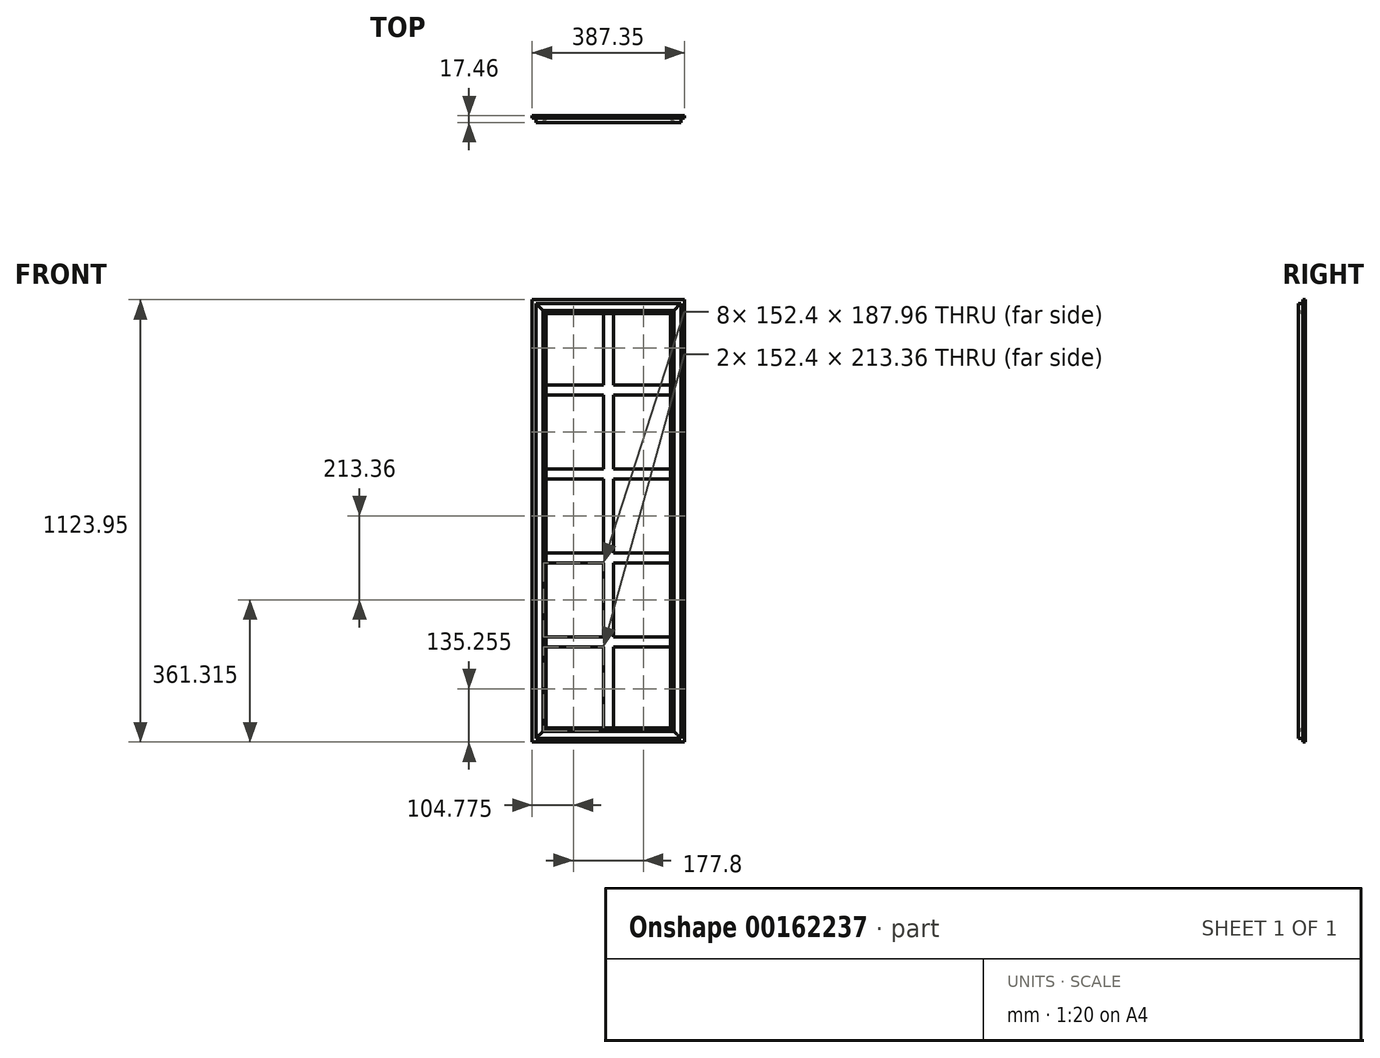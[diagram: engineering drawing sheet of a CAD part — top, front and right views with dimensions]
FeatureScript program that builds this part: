
annotation { "Feature Type Name" : "Feature", "Feature Type Description" : "" }
export const myFeature = defineFeature(function(context is Context, id is Id, definition is map)
    precondition{}
    {
        {
            var Q0;
            Q0=qCreatedBy(makeId("Front.planeOp"),FACE);
            var sketch = newSketch(context, id + "F0", { "sketchPlane" : qUnion([Q0])});
            skLineSegment(sketch, "E0.bottom", {"start": v(0, 1123.95) * mm, "end": v(387.35, 1123.95) * mm});
            skLineSegment(sketch, "E0.top", {"start": v(0, 0) * mm, "end": v(387.35, 0) * mm});
            skLineSegment(sketch, "E0.left", {"start": v(0, 1123.95) * mm, "end": v(0, 0) * mm});
            skLineSegment(sketch, "E0.right", {"start": v(387.35, 1123.95) * mm, "end": v(387.35, 0) * mm});
            skSolve(sketch);
        }
        {
            var Q0;
            Q0=qSketchRegion(id+"F0",true);
            extrude(context, id + "F1", {"entities" : qUnion([Q0]), "depth" : 6.35 * mm});
        }
        {
            var Q0;
            Q0=makeQuery(id+"F1.opExtrude","CAP_FACE",FACE,{"disambiguationData":[OSD([sQuery(id+"F0.wireOp",EDGE,"E0.bottom"),sQuery(id+"F0.wireOp",EDGE,"E0.top"),sQuery(id+"F0.wireOp",EDGE,"E0.left"),sQuery(id+"F0.wireOp",EDGE,"E0.right")])],"isStart":false});
            var sketch = newSketch(context, id + "F2", { "sketchPlane" : qUnion([Q0])});
            skLineSegment(sketch, "E1.0", {"start": v(6.35, 1117.6) * mm, "end": v(6.35, 6.35) * mm});
            skLineSegment(sketch, "E1.1", {"start": v(6.35, 1117.6) * mm, "end": v(381, 1117.6) * mm});
            skLineSegment(sketch, "E1.2", {"start": v(381, 1117.6) * mm, "end": v(381, 6.35) * mm});
            skLineSegment(sketch, "E2", {"start": v(6.35, 6.35) * mm, "end": v(381, 6.35) * mm});
            skSolve(sketch);
        }
        {
            var Q0;
            Q0=qCreatedBy(makeId("Front.planeOp"),FACE);
            var sketch = newSketch(context, id + "F3", { "sketchPlane" : qUnion([Q0])});
            skLineSegment(sketch, "E3.bottom", {"start": v(28.57, 1095.38) * mm, "end": v(358.77, 1095.38) * mm});
            skLineSegment(sketch, "E3.top", {"start": v(28.58, 28.58) * mm, "end": v(358.78, 28.58) * mm});
            skLineSegment(sketch, "E3.left", {"start": v(28.57, 1095.38) * mm, "end": v(28.58, 28.58) * mm});
            skLineSegment(sketch, "E3.right", {"start": v(358.77, 1095.38) * mm, "end": v(358.78, 28.58) * mm});
            skLineSegment(sketch, "E4", {"start": v(193.67, 1120.83) * mm, "end": v(193.67, 1069.4) * mm, "construction": true});
            skPoint(sketch, "E4.startSnap0", {"position": v(193.67, 1095.38) * mm});
            skSolve(sketch);
        }
        {
            var Q0;
            Q0=qCreatedBy(makeId("Front.planeOp"),FACE);
            var sketch = newSketch(context, id + "F4", { "sketchPlane" : qUnion([Q0])});
            skLineSegment(sketch, "E5.bottom", {"start": v(180.97, 1095.38) * mm, "end": v(206.37, 1095.38) * mm});
            skLineSegment(sketch, "E5.top", {"start": v(180.97, 28.58) * mm, "end": v(206.38, 28.58) * mm});
            skLineSegment(sketch, "E5.left", {"start": v(180.97, 1095.38) * mm, "end": v(180.97, 28.58) * mm});
            skLineSegment(sketch, "E5.right", {"start": v(206.37, 1095.38) * mm, "end": v(206.37, 28.58) * mm});
            skLineSegment(sketch, "E6.bottom", {"start": v(28.57, 907.41) * mm, "end": v(358.77, 907.41) * mm});
            skLineSegment(sketch, "E6.top", {"start": v(28.57, 882.01) * mm, "end": v(358.78, 882.01) * mm});
            skLineSegment(sketch, "E6.left", {"start": v(28.57, 907.41) * mm, "end": v(28.57, 882.01) * mm});
            skLineSegment(sketch, "E6.right", {"start": v(358.78, 907.41) * mm, "end": v(358.78, 882.01) * mm});
            skLineSegment(sketch, "E7.0.1.0", {"start": v(28.57, 668.65) * mm, "end": v(358.78, 668.65) * mm});
            skLineSegment(sketch, "E7.0.1.1", {"start": v(28.57, 694.05) * mm, "end": v(358.77, 694.05) * mm});
            skLineSegment(sketch, "E7.0.1.2", {"start": v(28.57, 694.05) * mm, "end": v(28.57, 668.65) * mm});
            skLineSegment(sketch, "E7.0.1.3", {"start": v(358.78, 694.05) * mm, "end": v(358.78, 668.65) * mm});
            skLineSegment(sketch, "E7.direction1", {"start": v(23.9, 882.01) * mm, "end": v(28.57, 882.01) * mm, "construction": true});
            skLineSegment(sketch, "E7.direction2", {"start": v(28.57, 882.01) * mm, "end": v(28.57, 668.65) * mm, "construction": true});
            skLineSegment(sketch, "E8.0.0.2", {"start": v(28.57, 455.3) * mm, "end": v(358.78, 455.3) * mm});
            skLineSegment(sketch, "E8.3.0.2", {"start": v(28.58, 480.7) * mm, "end": v(358.78, 480.7) * mm});
            skLineSegment(sketch, "E8.6.0.2", {"start": v(28.58, 480.7) * mm, "end": v(28.58, 455.3) * mm});
            skLineSegment(sketch, "E8.9.0.2", {"start": v(358.78, 480.7) * mm, "end": v(358.78, 455.3) * mm});
            skLineSegment(sketch, "E8.0.0.3", {"start": v(28.58, 241.93) * mm, "end": v(358.78, 241.93) * mm});
            skLineSegment(sketch, "E8.3.0.3", {"start": v(28.58, 267.33) * mm, "end": v(358.78, 267.33) * mm});
            skLineSegment(sketch, "E8.6.0.3", {"start": v(28.58, 267.33) * mm, "end": v(28.58, 241.93) * mm});
            skLineSegment(sketch, "E8.9.0.3", {"start": v(358.78, 267.33) * mm, "end": v(358.78, 241.93) * mm});
            skSolve(sketch);
        }
        {
            var Q0;
            Q0=makeQuery(id+"F2.imprint","IMPRINT",FACE,{"disambiguationData":[TD([[makeQuery(id+"F2.imprint","IMPRINT",EDGE,{"derivedFrom":sQuery(id+"F2.wireOp",EDGE,"E1.0")}),1.0]])]});
            var sketch = newSketch(context, id + "F5", { "sketchPlane" : qUnion([Q0])});
            skLineSegment(sketch, "E9.0", {"start": v(28.57, 1095.38) * mm, "end": v(180.97, 1095.38) * mm});
            skLineSegment(sketch, "E10.0", {"start": v(28.57, 1095.38) * mm, "end": v(28.57, 907.41) * mm});
            skLineSegment(sketch, "E11.0", {"start": v(180.97, 1095.38) * mm, "end": v(180.97, 907.41) * mm});
            skLineSegment(sketch, "E12.0", {"start": v(206.37, 1095.38) * mm, "end": v(206.37, 907.41) * mm});
            skLineSegment(sketch, "E13.0", {"start": v(358.77, 1095.38) * mm, "end": v(358.78, 907.41) * mm});
            skLineSegment(sketch, "E14.0", {"start": v(28.57, 907.41) * mm, "end": v(180.97, 907.41) * mm});
            skLineSegment(sketch, "E15.0", {"start": v(28.57, 882.01) * mm, "end": v(180.97, 882.01) * mm});
            skLineSegment(sketch, "E16.0", {"start": v(28.57, 694.05) * mm, "end": v(180.97, 694.05) * mm});
            skLineSegment(sketch, "E17.0", {"start": v(28.57, 668.65) * mm, "end": v(180.97, 668.65) * mm});
            skLineSegment(sketch, "E18.0", {"start": v(28.58, 480.7) * mm, "end": v(180.97, 480.7) * mm});
            skLineSegment(sketch, "E19.0", {"start": v(28.57, 455.3) * mm, "end": v(180.97, 455.3) * mm});
            skLineSegment(sketch, "E20.0", {"start": v(28.58, 267.33) * mm, "end": v(180.97, 267.33) * mm});
            skLineSegment(sketch, "E21.0", {"start": v(28.58, 241.93) * mm, "end": v(180.97, 241.93) * mm});
            skLineSegment(sketch, "E22.0", {"start": v(28.58, 28.58) * mm, "end": v(180.97, 28.58) * mm});
            skLineSegment(sketch, "E23.trimOffspring", {"start": v(206.37, 267.33) * mm, "end": v(358.78, 267.33) * mm});
            skLineSegment(sketch, "E24.trimOffspring", {"start": v(206.37, 241.93) * mm, "end": v(206.37, 28.58) * mm});
            skLineSegment(sketch, "E25.trimOffspring", {"start": v(180.97, 241.93) * mm, "end": v(180.97, 28.58) * mm});
            skLineSegment(sketch, "E26.trimOffspring", {"start": v(28.57, 241.93) * mm, "end": v(28.58, 28.58) * mm});
            skLineSegment(sketch, "E27.trimOffspring", {"start": v(206.37, 241.93) * mm, "end": v(358.78, 241.93) * mm});
            skLineSegment(sketch, "E28.trimOffspring", {"start": v(358.78, 241.93) * mm, "end": v(358.78, 28.58) * mm});
            skLineSegment(sketch, "E29.trimOffspring", {"start": v(206.37, 455.3) * mm, "end": v(358.78, 455.3) * mm});
            skLineSegment(sketch, "E30.trimOffspring", {"start": v(180.97, 455.3) * mm, "end": v(180.97, 267.33) * mm});
            skLineSegment(sketch, "E31.trimOffspring", {"start": v(206.37, 480.7) * mm, "end": v(358.78, 480.7) * mm});
            skLineSegment(sketch, "E32.trimOffspring", {"start": v(206.37, 455.3) * mm, "end": v(206.37, 267.33) * mm});
            skLineSegment(sketch, "E33.trimOffspring", {"start": v(358.78, 455.3) * mm, "end": v(358.78, 267.33) * mm});
            skLineSegment(sketch, "E34.trimOffspring", {"start": v(28.57, 455.3) * mm, "end": v(28.57, 267.33) * mm});
            skLineSegment(sketch, "E35.trimOffspring", {"start": v(206.37, 28.58) * mm, "end": v(358.78, 28.58) * mm});
            skLineSegment(sketch, "E36.trimOffspring", {"start": v(206.37, 668.66) * mm, "end": v(358.78, 668.66) * mm});
            skLineSegment(sketch, "E37.trimOffspring", {"start": v(206.37, 694.05) * mm, "end": v(358.77, 694.05) * mm});
            skLineSegment(sketch, "E38.trimOffspring", {"start": v(180.97, 668.65) * mm, "end": v(180.97, 480.7) * mm});
            skLineSegment(sketch, "E39.trimOffspring", {"start": v(206.37, 668.66) * mm, "end": v(206.37, 480.7) * mm});
            skLineSegment(sketch, "E40.trimOffspring", {"start": v(358.78, 668.65) * mm, "end": v(358.78, 480.7) * mm});
            skLineSegment(sketch, "E41.trimOffspring", {"start": v(28.57, 668.65) * mm, "end": v(28.57, 480.7) * mm});
            skLineSegment(sketch, "E42.trimOffspring", {"start": v(206.37, 882.02) * mm, "end": v(358.78, 882.02) * mm});
            skLineSegment(sketch, "E43.trimOffspring", {"start": v(206.37, 1095.38) * mm, "end": v(358.77, 1095.38) * mm});
            skLineSegment(sketch, "E44.trimOffspring", {"start": v(28.57, 882.01) * mm, "end": v(28.57, 694.05) * mm});
            skLineSegment(sketch, "E45.trimOffspring", {"start": v(206.37, 882.02) * mm, "end": v(206.37, 694.05) * mm});
            skLineSegment(sketch, "E46.trimOffspring", {"start": v(206.37, 907.41) * mm, "end": v(358.77, 907.41) * mm});
            skLineSegment(sketch, "E47.trimOffspring", {"start": v(180.97, 882.01) * mm, "end": v(180.97, 694.05) * mm});
            skLineSegment(sketch, "E48.trimOffspring", {"start": v(358.78, 882.01) * mm, "end": v(358.78, 694.05) * mm});
            skSolve(sketch);
        }
        {
            var Q0;
            Q0 = qSketchRegion(id + "F5", true);
            extrude(context, id + "F6", {"entities" : qUnion([Q0]), "operationType" : NewBodyOperationType.REMOVE, "oppositeDirection" : true, "depth" : 12.7 * mm});
        }
        {
            var Q0;
            Q0=makeQuery(id+"F2.imprint","IMPRINT",FACE,{"disambiguationData":[TD([[makeQuery(id+"F2.imprint","IMPRINT",EDGE,{"derivedFrom":sQuery(id+"F2.wireOp",EDGE,"E1.0")}),-1.0]])]});
            var sketch = newSketch(context, id + "F7", { "sketchPlane" : qUnion([Q0])});
            skLineSegment(sketch, "E49.bottom", {"start": v(9.52, 1114.42) * mm, "end": v(377.83, 1114.42) * mm});
            skLineSegment(sketch, "E49.top", {"start": v(9.53, 9.53) * mm, "end": v(377.83, 9.53) * mm});
            skLineSegment(sketch, "E49.left", {"start": v(9.52, 1114.42) * mm, "end": v(9.53, 9.53) * mm});
            skLineSegment(sketch, "E49.right", {"start": v(377.83, 1114.42) * mm, "end": v(377.83, 9.53) * mm});
            skSolve(sketch);
        }
        {
            var Q0;
            Q0=sQuery(id+"F7.wireOp",VERTEX,"E49.right.start");
            var Q1;
            Q1=sQuery(id+"F7.wireOp",EDGE,"E49.right");
            cPlane(context, id + "F8", {"entities" : qUnion([Q0, Q1]), "cplaneType" : CPlaneType.LINE_POINT, "offset" : 25.4 * mm, "width" : 152.4 * mm, "height" : 152.4 * mm});
        }
        {
            var Q0;
            Q0=qCreatedBy(id+"F8.planeOp",FACE);
            var sketch = newSketch(context, id + "F9", { "sketchPlane" : qUnion([Q0])});
            skLineSegment(sketch, "E50", {"start": v(377.83, 6.35) * mm, "end": v(360.36, 6.35) * mm});
            skLineSegment(sketch, "E51", {"start": v(377.83, 17.46) * mm, "end": v(377.83, 6.35) * mm});
            skFitSpline(sketch, "E52", {"points": [v(377.83, 17.46) * mm, v(361.9, 15.42) * mm, v(357.76, 12.2) * mm, v(352.01, 9.86) * mm, v(360.36, 6.35) * mm], "startDerivative": vector(-23.13, 0) * mm, "endDerivative": vector(-0.82, -20.64) * mm});
            skSolve(sketch);
        }
        {
            var Q0;
            Q0=makeQuery(id+"F9.imprint","IMPRINT",FACE,{"disambiguationData":[TD([[makeQuery(id+"F9.imprint","IMPRINT",EDGE,{"derivedFrom":sQuery(id+"F9.wireOp",EDGE,"E50")}),-1.0]])]});
            var Q1;
            Q1=sQuery(id+"F7.wireOp",EDGE,"E49.right");
            var Q2;
            Q2=sQuery(id+"F7.wireOp",EDGE,"E49.top");
            var Q3;
            Q3=sQuery(id+"F7.wireOp",EDGE,"E49.left");
            var Q4;
            Q4=sQuery(id+"F7.wireOp",EDGE,"E49.bottom");
            sweep(context, id + "F10", {"operationType" : NewBodyOperationType.ADD, "profiles" : qUnion([Q0]), "path" : qUnion([Q1, Q2, Q3, Q4])});
        }
    });
